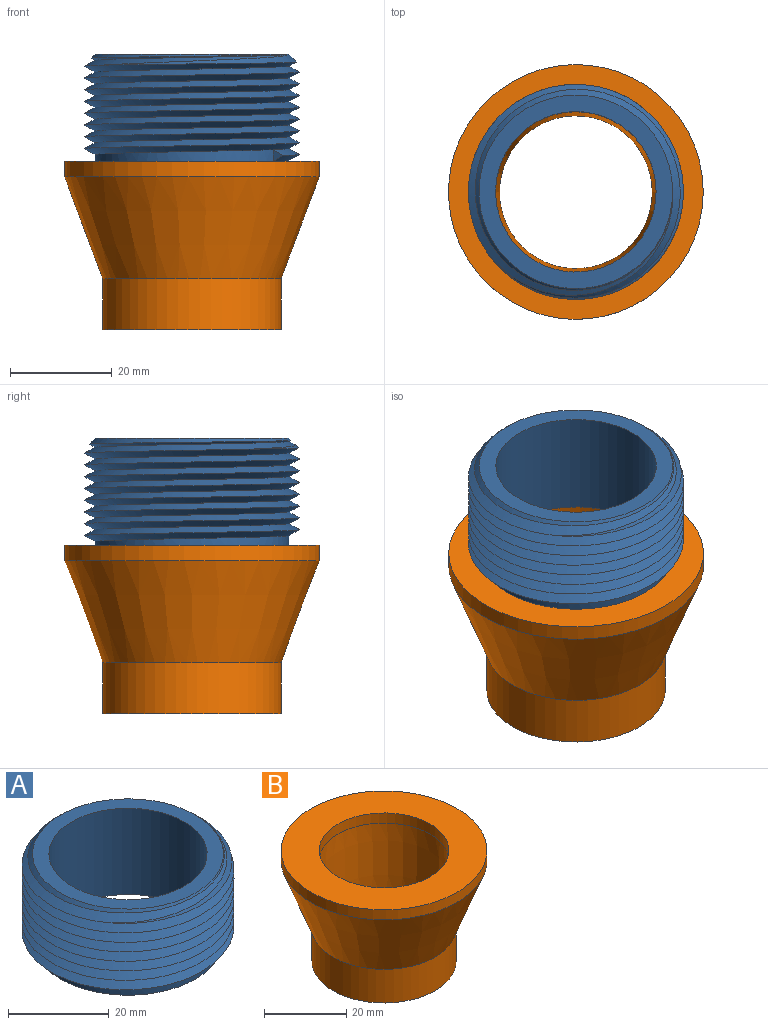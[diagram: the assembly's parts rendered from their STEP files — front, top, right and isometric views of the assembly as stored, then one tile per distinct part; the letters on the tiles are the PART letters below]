
ASSEMBLY  parts=2 mates=1
PART A: 8 faces, bbox 42.2x48.7x22.3 mm
  f0: bspline ~48.73x42.2mm, area 2538.6mm2, adj f1,f3,f5,f6,f7
  f1: bspline ~48.73x42.2mm, area 2379.8mm2, adj f0,f3,f6,f7
  f2: cylinder r=15.75mm len=31.5mm, axis (0,0,-1), area 2078.2mm2, adj f4,f5
  f3: cylinder r=19mm len=38mm, axis (0,0,-1), area 130.7mm2, adj f0,f1,f4,f5,f6
  f4: plane 38x38mm, normal (0,0,1), area 354.8mm2, adj f2,f3,f7
  f5: plane 38x38mm, normal (0,0,-1), area 354.8mm2, adj f0,f2,f3
  f6: plane 2.3x1.77mm, normal (-0.54,-0.84,0), area 2.4mm2, adj f0,f1,f3
  f7: cone r=19mm half-angle=45deg, axis (0,0,-1), area 183.1mm2, adj f0,f1,f4
PART B: 8 faces, bbox 50x50x33 mm
  f0: plane 50x50mm, normal (0,0,1), area 1184.2mm2, adj f1,f7
  f1: cylinder r=15.75mm len=31.5mm, axis (0,0,1), area 296.9mm2, adj f0,f2
  f2: cone r=15.75mm half-angle=2.1deg, axis (0,0,1), area 1933.4mm2, adj f1,f3
  f3: cylinder r=15mm len=30mm, axis (0,0,1), area 942.5mm2, adj f2,f4
  f4: plane 35x35mm, normal (0,0,-1), area 255.3mm2, adj f3,f5
  f5: cylinder r=17.5mm len=35mm, axis (0,0,1), area 1099.6mm2, adj f4,f6
  f6: cone r=17.5mm half-angle=20.6deg, axis (0,0,1), area 2851.9mm2, adj f5,f7
  f7: cylinder r=25mm len=50mm, axis (0,0,1), area 471.2mm2, adj f0,f6
PLACE A t=(2.87,4.81,-16.8)mm
PLACE B t=(2.87,4.81,-49.8)mm
MATE fastened A.f2 <-> B.f1  axis (0,0,-1) through (2.87,4.81,-16.8)mm
